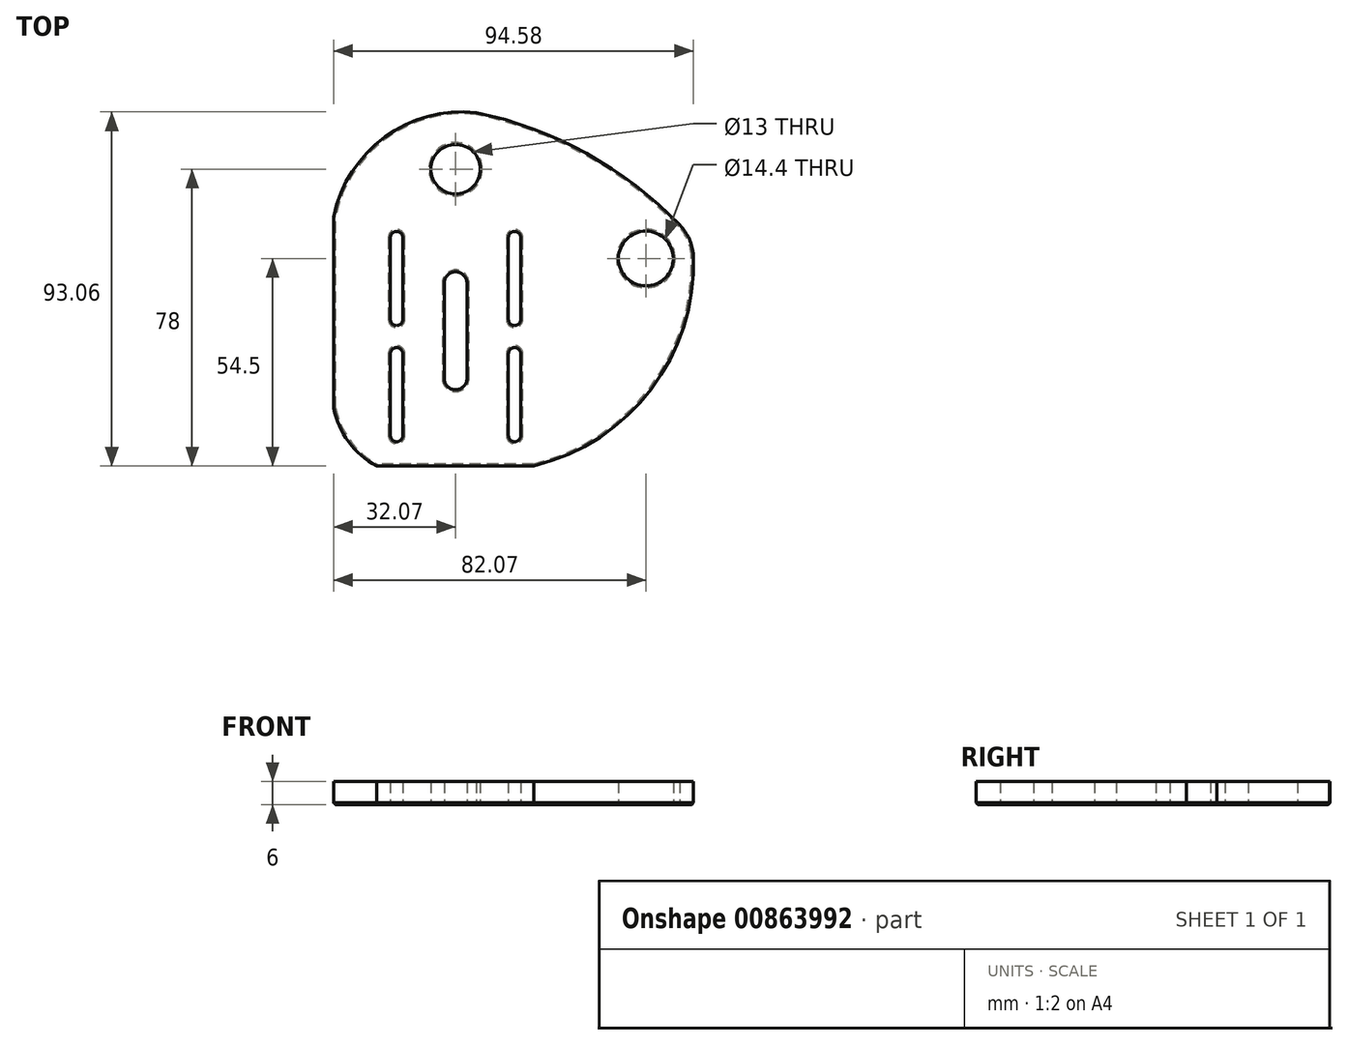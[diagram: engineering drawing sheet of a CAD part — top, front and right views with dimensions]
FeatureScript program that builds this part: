
annotation { "Feature Type Name" : "Feature", "Feature Type Description" : "" }
export const myFeature = defineFeature(function(context is Context, id is Id, definition is map)
    precondition{}
    {
        {
            var Q0;
            Q0=qCreatedBy(makeId("Top.planeOp"),FACE);
            var sketch = newSketch(context, id + "F0", { "sketchPlane" : qUnion([Q0])});
            skLineSegment(sketch, "E0.left", {"start": v(-36, 31.5) * mm, "end": v(-36, -33.5) * mm});
            skLineSegment(sketch, "E0.right", {"start": v(-5, 31.5) * mm, "end": v(-5, -33.5) * mm});
            skPoint(sketch, "E0.middle", {"position": v(-20.5, -11) * mm});
            skLineSegment(sketch, "E1", {"start": v(-5, 31.5) * mm, "end": v(29.5, 31.5) * mm});
            skLineSegment(sketch, "E2", {"start": v(29.5, 31.5) * mm, "end": v(29.5, 8) * mm});
            skCircle(sketch, "E3", {"center": v(-20.5, 31.5) * mm, "radius": 6.5 * mm});
            skCircle(sketch, "E4", {"center": v(29.5, 8) * mm, "radius": 7.2 * mm});
            skLineSegment(sketch, "E5.left", {"start": v(-17.5, 1.5) * mm, "end": v(-17.5, -23.5) * mm});
            skLineSegment(sketch, "E5.right", {"start": v(-23.5, 1.5) * mm, "end": v(-23.5, -23.5) * mm});
            skArc(sketch, "E6", {"start": v(-23.5, -23.5) * mm, "mid": v(-20.5, -26.5) * mm, "end": v(-17.5, -23.5) * mm});
            skArc(sketch, "E7", {"start": v(-17.5, 1.5) * mm, "mid": v(-20.5, 4.5) * mm, "end": v(-23.5, 1.5) * mm});
            skLineSegment(sketch, "E8", {"start": v(-5, 31.5) * mm, "end": v(-20.5, 31.5) * mm});
            skLineSegment(sketch, "E9", {"start": v(-20.5, 31.5) * mm, "end": v(-36, 31.5) * mm});
            skLineSegment(sketch, "E10", {"start": v(-20.5, 1.5) * mm, "end": v(-20.5, 31.5) * mm});
            skLineSegment(sketch, "E11", {"start": v(0, 0) * mm, "end": v(-5, 0) * mm});
            skSolve(sketch);
        }
        {
            var Q0;
            Q0=qCreatedBy(makeId("Top.planeOp"),FACE);
            var sketch = newSketch(context, id + "F1", { "sketchPlane" : qUnion([Q0])});
            skLineSegment(sketch, "E12", {"start": v(-6.63, -8) * mm, "end": v(-6.63, 13.5) * mm});
            skLineSegment(sketch, "E13", {"start": v(-3.37, -17.02) * mm, "end": v(-3.37, -38.53) * mm});
            skArc(sketch, "E14", {"start": v(-3.37, 13.5) * mm, "mid": v(-5, 15.13) * mm, "end": v(-6.63, 13.5) * mm});
            skArc(sketch, "E15", {"start": v(-6.63, -8) * mm, "mid": v(-5, -9.63) * mm, "end": v(-3.37, -8) * mm});
            skArc(sketch, "E16", {"start": v(-3.37, -17.02) * mm, "mid": v(-5, -15.4) * mm, "end": v(-6.63, -17.02) * mm});
            skLineSegment(sketch, "E17", {"start": v(-6.63, -38.53) * mm, "end": v(-6.63, -38.53) * mm});
            skLineSegment(sketch, "E18", {"start": v(-3.37, 13.5) * mm, "end": v(-3.37, -8) * mm});
            skLineSegment(sketch, "E19", {"start": v(-6.63, 13.5) * mm, "end": v(-6.63, 13.5) * mm});
            skLineSegment(sketch, "E20", {"start": v(-3.37, -38.53) * mm, "end": v(-3.37, -38.53) * mm});
            skArc(sketch, "E21", {"start": v(-6.63, -38.53) * mm, "mid": v(-5, -40.15) * mm, "end": v(-3.37, -38.53) * mm});
            skLineSegment(sketch, "E22", {"start": v(-6.63, -38.53) * mm, "end": v(-6.63, -17.02) * mm});
            skLineSegment(sketch, "E23", {"start": v(-5, 13.5) * mm, "end": v(-5, -8) * mm});
            skLineSegment(sketch, "E24", {"start": v(-5, 13.5) * mm, "end": v(0, 13.5) * mm});
            skLineSegment(sketch, "E25", {"start": v(0, 13.5) * mm, "end": v(0, 0) * mm});
            skLineSegment(sketch, "E26", {"start": v(-5, -8) * mm, "end": v(-5, -17.02) * mm});
            skLineSegment(sketch, "E27", {"start": v(-5, -17.02) * mm, "end": v(-5, -38.53) * mm});
            skArc(sketch, "E28.MirrorCS", {"start": v(-34.37, -38.53) * mm, "mid": v(-36, -40.15) * mm, "end": v(-37.63, -38.53) * mm});
            skArc(sketch, "E29.MirrorCS", {"start": v(-34.37, -8) * mm, "mid": v(-36, -9.63) * mm, "end": v(-37.63, -8) * mm});
            skArc(sketch, "E30.MirrorCS", {"start": v(-37.63, 13.5) * mm, "mid": v(-36, 15.13) * mm, "end": v(-34.37, 13.5) * mm});
            skArc(sketch, "E31.MirrorCS", {"start": v(-37.63, -17.02) * mm, "mid": v(-36, -15.4) * mm, "end": v(-34.37, -17.02) * mm});
            skLineSegment(sketch, "E32.MirrorCS", {"start": v(-34.37, -38.53) * mm, "end": v(-34.37, -38.53) * mm});
            skLineSegment(sketch, "E33.MirrorCS", {"start": v(-37.63, -38.53) * mm, "end": v(-37.63, -38.53) * mm});
            skLineSegment(sketch, "E34.MirrorCS", {"start": v(-36, 13.5) * mm, "end": v(-41, 13.5) * mm});
            skLineSegment(sketch, "E35.MirrorCS", {"start": v(-34.37, 13.5) * mm, "end": v(-34.37, 13.5) * mm});
            skLineSegment(sketch, "E36.MirrorCS", {"start": v(-36, 13.5) * mm, "end": v(-36, -8) * mm});
            skLineSegment(sketch, "E37.MirrorCS", {"start": v(-34.37, -38.53) * mm, "end": v(-34.37, -17.02) * mm});
            skLineSegment(sketch, "E38.MirrorCS", {"start": v(-41, 13.5) * mm, "end": v(-41, 0) * mm});
            skLineSegment(sketch, "E39.MirrorCS", {"start": v(-36, -17.02) * mm, "end": v(-36, -38.53) * mm});
            skLineSegment(sketch, "E40.MirrorCS", {"start": v(-37.63, -17.02) * mm, "end": v(-37.63, -38.53) * mm});
            skLineSegment(sketch, "E41.MirrorCS", {"start": v(-36, -8) * mm, "end": v(-36, -17.02) * mm});
            skLineSegment(sketch, "E42.MirrorCS", {"start": v(-37.63, 13.5) * mm, "end": v(-37.63, -8) * mm});
            skLineSegment(sketch, "E43.MirrorCS", {"start": v(-34.37, -8) * mm, "end": v(-34.37, 13.5) * mm});
            skSolve(sketch);
        }
        {
            var Q0;
            Q0=qCreatedBy(makeId("Top.planeOp"),FACE);
            var sketch = newSketch(context, id + "F2", { "sketchPlane" : qUnion([Q0])});
            skArc(sketch, "E44", {"start": v(38.36, 16.81) * mm, "mid": v(13.89, 35.6) * mm, "end": v(-15.03, 46.37) * mm});
            skArc(sketch, "E45", {"start": v(-15.03, 46.37) * mm, "mid": v(-39.1, 39.91) * mm, "end": v(-52.57, 18.94) * mm});
            skArc(sketch, "E46", {"start": v(-52.5, -31.3) * mm, "mid": v(-48.62, -40.17) * mm, "end": v(-41.29, -46.5) * mm});
            skLineSegment(sketch, "E47", {"start": v(-52.5, -31.3) * mm, "end": v(-52.57, 18.94) * mm});
            skArc(sketch, "E48", {"start": v(0, -46.5) * mm, "mid": v(30.87, -26.36) * mm, "end": v(41.98, 8.78) * mm});
            skArc(sketch, "E49", {"start": v(41.98, 8.78) * mm, "mid": v(40.9, 13.12) * mm, "end": v(38.36, 16.81) * mm});
            skLineSegment(sketch, "E50", {"start": v(-41.29, -46.5) * mm, "end": v(0, -46.5) * mm});
            skSolve(sketch);
        }
        {
            var Q0;
            Q0 = qSketchRegion(id + "F2", true);
            extrude(context, id + "F3", {"entities" : qUnion([Q0]), "depth" : 6 * mm, "offsetDistance" : 25 * mm});
        }
        {
            var Q0;
            Q0 = qSketchRegion(id + "F0", true);
            extrude(context, id + "F4", {"entities" : qUnion([Q0]), "operationType" : NewBodyOperationType.REMOVE, "oppositeDirection" : true, "depth" : -6 * mm, "offsetDistance" : 25 * mm});
        }
        {
            var Q0;
            Q0 = qSketchRegion(id + "F1", true);
            extrude(context, id + "F5", {"entities" : qUnion([Q0]), "operationType" : NewBodyOperationType.REMOVE, "oppositeDirection" : true, "depth" : -6 * mm, "offsetDistance" : 25 * mm});
        }
        {
            var Q0;
            Q0=makeQuery(id+"F3.opExtrude","CAP_EDGE",EDGE,{"disambiguationData":[OSD([sQuery(id+"F2.wireOp",EDGE,"E48")])],"isStart":true});
            var Q1;
            Q1=makeQuery(id+"F3.opExtrude","CAP_FACE",FACE,{"disambiguationData":[OSD([sQuery(id+"F2.wireOp",EDGE,"E44"),sQuery(id+"F2.wireOp",EDGE,"E45"),sQuery(id+"F2.wireOp",EDGE,"E46"),sQuery(id+"F2.wireOp",EDGE,"E47"),sQuery(id+"F2.wireOp",EDGE,"E48"),sQuery(id+"F2.wireOp",EDGE,"E49"),sQuery(id+"F2.wireOp",EDGE,"E50")])],"isStart":true});
            chamfer(context, id + "F6", {"entities" : qUnion([Q0, Q1]), "chamferType" : ChamferType.OFFSET_ANGLE, "width" : 0.5 * mm, "oppositeDirection" : false, "angle" : 45 * degree, "tangentPropagation" : true});
        }
    });
